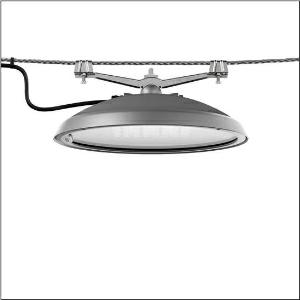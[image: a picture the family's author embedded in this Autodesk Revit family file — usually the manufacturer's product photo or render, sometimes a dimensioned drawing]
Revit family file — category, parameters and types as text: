
# Revit family: dl_r__50_iq_mini___st1_0s_5xa248w21f08he_f114
name_source: partatom
category: Lighting Fixtures
units: mm (PartAtom-declared; Revit-internal decimal feet)

## family parameters
Cut with Voids When Loaded = No
Host = Face
Light Source = No
Part Type = Normal
Room Calculation Point = No
Round Connector Dimension = Use Diameter
Shared = No

## types (1)
- --- (1 x LED, 7840 lm, 69.3 W, 2200K)
    Apparent Load = 69 VA
    CIE Flux Codes = 37 72 97 100 100
    Color Rendering = 70
    Color Temperature = 2200K
    Default Elevation = 1800 mm
    Description = DL® 50 iQ mini, catenary luminaire, primary light control with lens, of PMMA, primary optical cover: cover, of toughened safety glass, transparent, light distribution: ST1.0s, light emission: direct distribution, primary light characteristic: symmetric, installation type: suspended mounting, LED, High Power LED, rated luminous flux: 7.840lm, luminous efficacy: 113lm/W, light colour: 722, colour temperature: 2200K, control: optimised constant luminous flux control (CLO 2.0), Desk-Remote (wireless, voltage-free reading and setting of iQ features in the workshop via application-optimized NFC function/RFID function), Light-Fading, Smart-Wire, Night-Set, Lumen-Switch, Temp-Guard, Auto-Match, Street-Remote, mains connection: 230..240V, AC, 50/60Hz, start of lifetime: 69W, end of service life: 74W, reduction: 30W, luminaire housing, of diecast aluminium, powder-coated, Siteco® metallic grey (DB 702S), diameter: 500mm, height: 115mm, protection rating (complete): IP66, insulation class (complete): insulation class II (safety insulation), certification: CE, ENEC, VDE, impact resistance: IK08, permissible operating ambient temperature for outdoor applications: -25..+40°C, standard-compliant lighting for roads and squares, packaging unit: 1 piece

Light Distribution: ST1.0s
    Height = 124 mm  [stored 0.406824 ft]
    Lamp = 1 x LED
    Lamp Light Flux = 7840 lm
    Lamp Power = 69.3 W
    Lamp count = 1
    Length = 500 mm
    Luminous efficacy = 113 lm/W
    Manufacturer = Siteco
    ModVariant = No
    Model = 5XA248W21F08HE
    Number of Poles = 1
    OnlyDefault = Yes
    Power Factor = 1
    Product Name = DL® 50 iQ mini | ST1.0s
    Product group = catenary luminaire
    ProductGroupID = 6300
    Protection Class = Protection class II
    Protection Degree = IP 66
    RLX_Detail_Level = 1
    RLX_Emergency_Light_Flux = 0 lm
    RLX_Emergency_Type = 0
    RLX_Emergency_Type_DB = No
    RlxData = <blob elided: 123289 chars, md5=8f61ab3f>
    Socket = socket
    Standby Power = 0 W
    System Light Flux = 7840 lm
    System Power = 69 W
    Type Comments = factory setting: luminous flux: 100 % | dim-lin: 254 | 700 mA
    Type Image = l_1242791.jpg
    URL = http://relux.com
    VarID = @adj_090047
    Voltage = 0 V
    Weight = 0.00 kg
    Width = 0 mm  [stored 0 ft]

note: [stored X ft] marks values corroborated as IEEE doubles in the binary element streams (Revit-internal decimal feet)

## geometry (parser evidence)
native form markers: Blend x4, Sweep x13
no freeform markers — native parametric forms only
